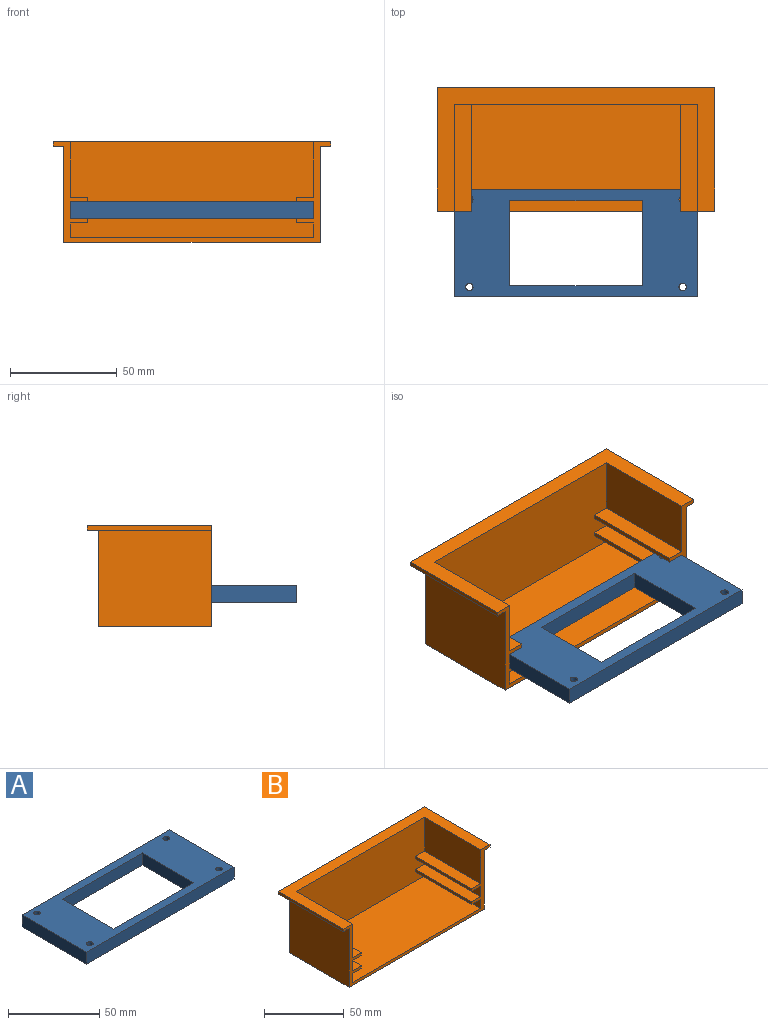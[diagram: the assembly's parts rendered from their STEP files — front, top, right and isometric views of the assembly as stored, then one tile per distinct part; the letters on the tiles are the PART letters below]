
ASSEMBLY  parts=2 mates=1
PART A: 14 faces, bbox 114x50x8 mm
  f0: plane 40x8mm, normal (1,0,0), area 320mm2, adj f1,f11,f12,f13
  f1: plane 62x8mm, normal (0,-1,0), area 496mm2, adj f0,f2,f12,f13
  f2: plane 40x8mm, normal (-1,0,0), area 320mm2, adj f1,f11,f12,f13
  f3: plane 114x8mm, normal (0,1,0), area 912mm2, adj f4,f6,f12,f13
  f4: plane 50x8mm, normal (-1,0,0), area 400mm2, adj f3,f5,f12,f13
  f5: plane 114x8mm, normal (0,-1,0), area 912mm2, adj f4,f6,f12,f13
  f6: plane 50x8mm, normal (1,0,0), area 400mm2, adj f3,f5,f12,f13
  f7: cylinder r=1.75mm len=8mm, axis (0,0,-1), area 88mm2, adj f12,f13
  f8: cylinder r=1.75mm len=8mm, axis (0,0,-1), area 88mm2, adj f12,f13
  f9: cylinder r=1.75mm len=8mm, axis (0,0,-1), area 88mm2, adj f12,f13
  f10: cylinder r=1.75mm len=8mm, axis (0,0,-1), area 88mm2, adj f12,f13
  f11: plane 62x8mm, normal (0,1,0), area 496mm2, adj f0,f2,f12,f13
  f12: plane 114x50mm, normal (0,0,1), area 3181.5mm2, adj f0,f1,f2,f3,f4,f5,f6,f7
  f13: plane 114x50mm, normal (0,0,-1), area 3181.5mm2, adj f0,f1,f2,f3,f4,f5,f6,f7
PART B: 30 faces, bbox 130x58x47 mm
  f0: plane 50x8mm, normal (-1,0,0), area 400mm2, adj f1,f5,f25,f29
  f1: plane 114x45mm, normal (0,-1,0), area 5066mm2, adj f0,f2,f3,f4,f6,f8,f9,f17
  f2: plane 50x7mm, normal (-1,0,0), area 350mm2, adj f1,f5,f6,f24
  f3: plane 50x7mm, normal (1,0,0), area 350mm2, adj f1,f5,f6,f21
  f4: plane 50x8mm, normal (1,0,0), area 400mm2, adj f1,f5,f19,f23
  f5: plane 130x47mm, normal (0,-1,0), area 594mm2, adj f0,f2,f3,f4,f6,f7,f8,f9
  f6: plane 114x50mm, normal (0,0,1), area 5700mm2, adj f1,f2,f3,f5
  f7: plane 120x53mm, normal (0,0,-1), area 6360mm2, adj f5,f10,f11,f12
  f8: plane 50x26mm, normal (1,0,0), area 1300mm2, adj f1,f5,f17,f18
  f9: plane 50x26mm, normal (-1,0,0), area 1300mm2, adj f1,f5,f17,f27
  f10: plane 53x45mm, normal (1,0,0), area 2385mm2, adj f5,f7,f11,f13
  f11: plane 120x45mm, normal (0,1,0), area 5400mm2, adj f7,f10,f12,f13
  f12: plane 53x45mm, normal (-1,0,0), area 2385mm2, adj f5,f7,f11,f13
  f13: plane 130x58mm, normal (0,0,-1), area 1180mm2, adj f5,f10,f11,f12,f14,f15,f16
  f14: plane 58x2mm, normal (1,0,0), area 116mm2, adj f5,f13,f15,f17
  f15: plane 130x2mm, normal (0,1,0), area 260mm2, adj f13,f14,f16,f17
  f16: plane 58x2mm, normal (-1,0,0), area 116mm2, adj f5,f13,f15,f17
  f17: plane 130x58mm, normal (0,0,1), area 1840mm2, adj f1,f5,f8,f9,f14,f15,f16
  f18: plane 50x8mm, normal (0,0,1), area 400mm2, adj f1,f5,f8,f20
  f19: plane 50x8mm, normal (0,0,-1), area 400mm2, adj f1,f4,f5,f20
  f20: plane 50x2mm, normal (1,0,0), area 100mm2, adj f1,f5,f18,f19
  f21: plane 50x8mm, normal (0,0,-1), area 400mm2, adj f1,f3,f5,f22
  f22: plane 50x2mm, normal (1,0,0), area 100mm2, adj f1,f5,f21,f23
  f23: plane 50x8mm, normal (0,0,1), area 400mm2, adj f1,f4,f5,f22
  f24: plane 50x8mm, normal (0,0,-1), area 400mm2, adj f1,f2,f5,f26
  f25: plane 50x8mm, normal (0,0,1), area 400mm2, adj f0,f1,f5,f26
  f26: plane 50x2mm, normal (-1,0,0), area 100mm2, adj f1,f5,f24,f25
  f27: plane 50x8mm, normal (0,0,1), area 400mm2, adj f1,f5,f9,f28
  f28: plane 50x2mm, normal (-1,0,0), area 100mm2, adj f1,f5,f27,f29
  f29: plane 50x8mm, normal (0,0,-1), area 400mm2, adj f0,f1,f5,f28
PLACE A t=(32.31,-89.8,42.91)mm
PLACE B t=(32.31,-49.8,31.91)mm
MATE planar A.f4 <-> B.f4  axis (-1,0,0) through (-24.69,-89.8,46.91)mm
